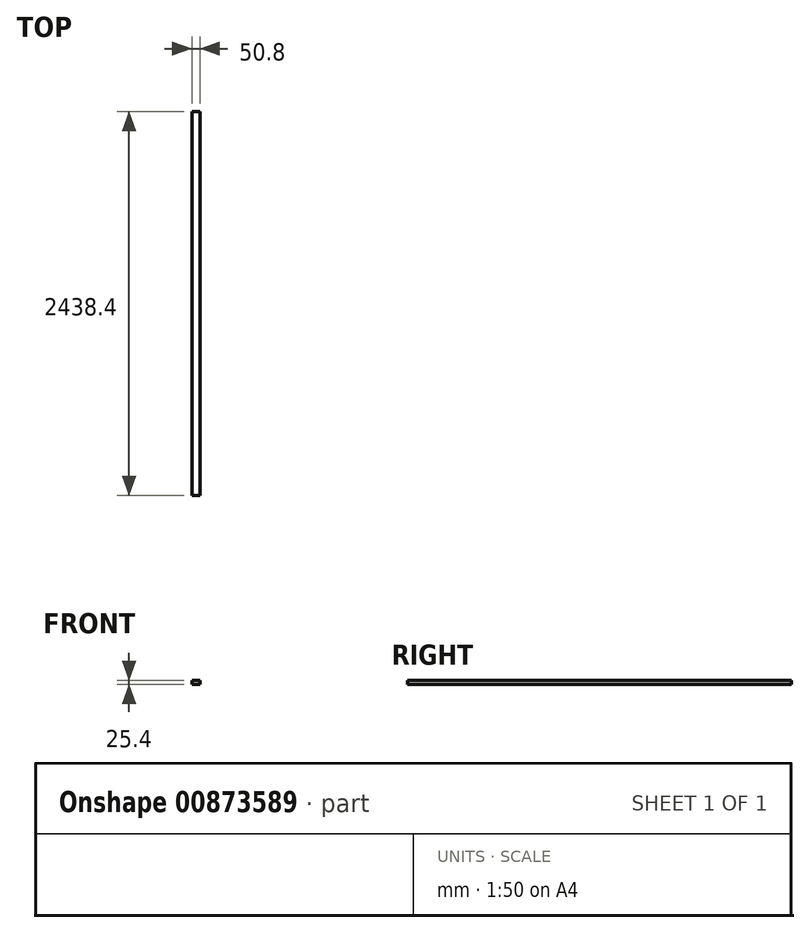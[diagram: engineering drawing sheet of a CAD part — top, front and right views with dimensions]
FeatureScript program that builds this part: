
annotation { "Feature Type Name" : "Feature", "Feature Type Description" : "" }
export const myFeature = defineFeature(function(context is Context, id is Id, definition is map)
    precondition{}
    {
        {
            var Q0;
            Q0=qCreatedBy(makeId("Top.planeOp"),FACE);
            var sketch = newSketch(context, id + "F0", { "sketchPlane" : qUnion([Q0])});
            skLineSegment(sketch, "E0.bottom", {"start": v(0, 0) * mm, "end": v(50.8, 0) * mm});
            skLineSegment(sketch, "E0.top", {"start": v(0, 2438.4) * mm, "end": v(50.8, 2438.4) * mm});
            skLineSegment(sketch, "E0.left", {"start": v(0, 0) * mm, "end": v(0, 2438.4) * mm});
            skLineSegment(sketch, "E0.right", {"start": v(50.8, 0) * mm, "end": v(50.8, 2438.4) * mm});
            skSolve(sketch);
        }
        {
            var Q0;
            Q0=qSketchRegion(id+"F0",true);
            extrude(context, id + "F1", {"entities" : qUnion([Q0]), "depth" : 25.4 * mm, "offsetDistance" : 25.4 * mm});
        }
    });
